# Revit family: FU_Inspec_Campus_Air_2-2
name_source: partatom
category: Furniture
units: mm (PartAtom-declared; Revit-internal decimal feet)

## family parameters
Always vertical = Yes
Cut with Voids When Loaded = No
OmniClass Number = 23.40.20.00
OmniClass Title = General Furniture and Specialties
Room Calculation Point = No
Shared = No
Work Plane-Based = No

## types (4) — shared parameters
Armrest Material = Plastic - Black
Assembly Code = E2020
Back Upholstery = Fabric - Black
Frame Material = Metal - Chrome - Polished
Keynote = 46.B
Manufacturer = Inspec
URL = https://inspecfurniture.com
Upholstered Back Visibility = No
zero-valued in all types: Default Elevation

## per-type parameters (varying)
| type | Arms Visibility | Back Material | Description | Model | Seat Material | Seat Upholstery | Seat Visibility | Upholstered Seat Visibility |
| Campus Air 2.1 | Yes | Polyamide - Blue Green | Armchair on a powder coated or chromium plated steel frame. Seat and back in glass-fibre reinforced polyamide. | Campus Air 2.1 | Polyamide - Blue Green | Fabric - Red | Yes | No |
| Campus Air 1.1 | No | Polyamide - Blue | Chair on a powder coated or chromium plated steel frame. Seat and back in glass-fibre reinforced polyamide. | Campus Air 1.1 | Polyamide - Blue | Fabric - Red | Yes | No |
| Campus Air 1.2 | No | Polyamide - White | Chair on a powder coated or chromium plated steel frame. Upholstered seat, back in glass-fibre reinforced polyamide. | Campus Air 1.2 | Polyamide - Blue | Fabric - Red | No | Yes |
| Campus Air 2.2 | Yes | Polyamide - White | Armchair on a powder coated or chromium plated steel frame. Upholstered seat, back in glass-fibre reinforced polyamide. | Campus Air 2.1 | Polyamide - Blue | Fabric - Black | No | Yes |

## geometry (parser evidence)
native form markers: Blend x10, Sweep x5
no freeform markers — native parametric forms only
